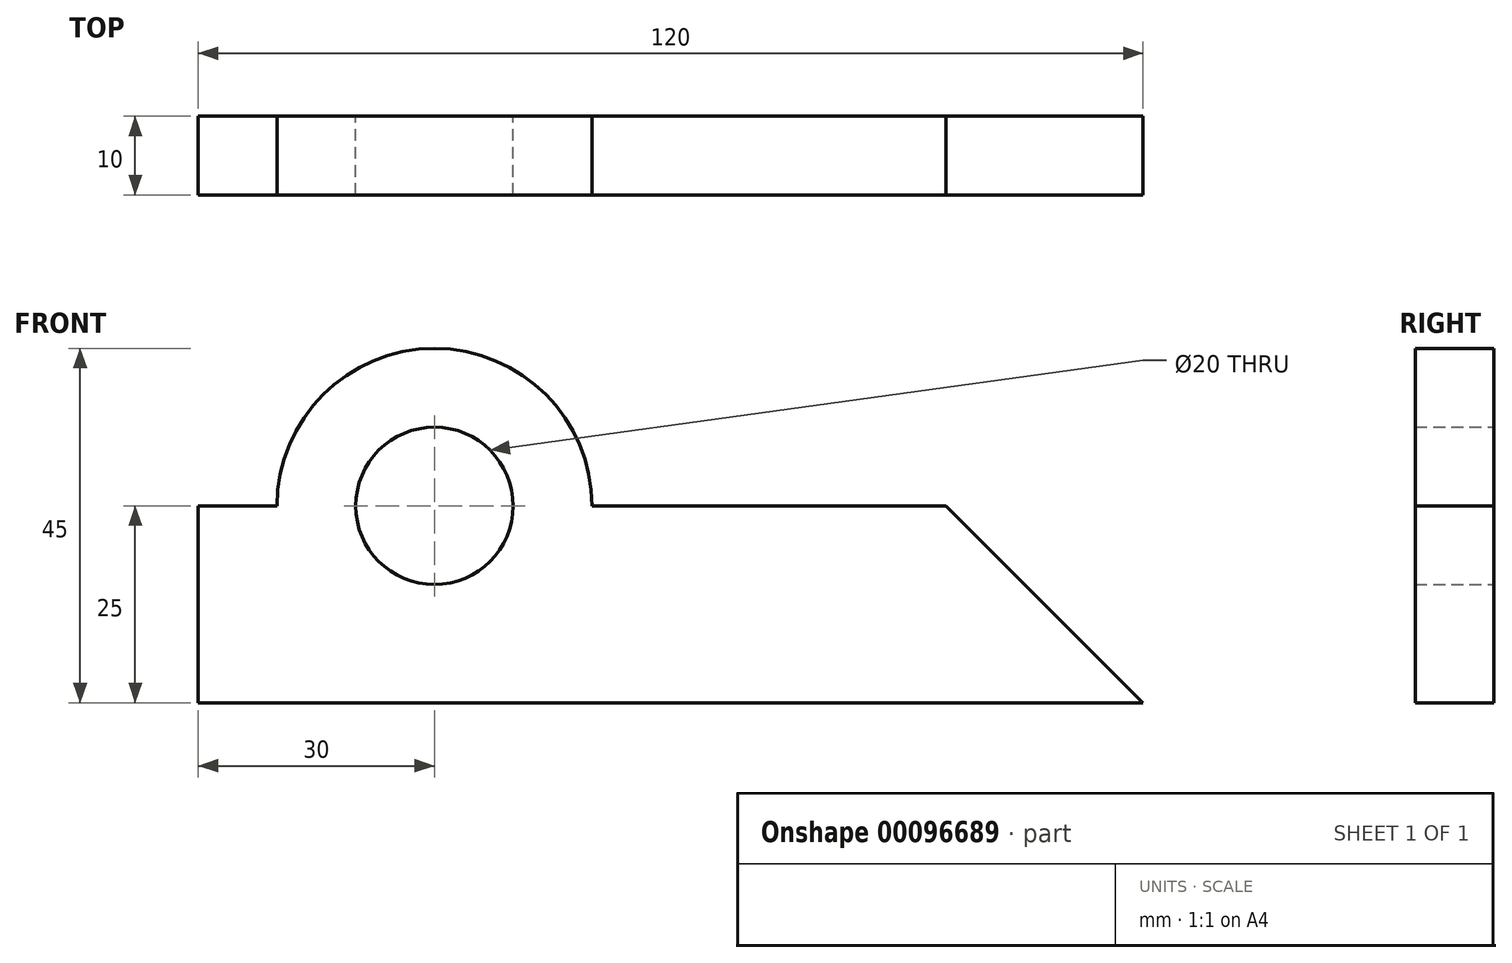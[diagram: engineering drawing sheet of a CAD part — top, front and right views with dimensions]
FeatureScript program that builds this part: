
annotation { "Feature Type Name" : "Feature", "Feature Type Description" : "" }
export const myFeature = defineFeature(function(context is Context, id is Id, definition is map)
    precondition{}
    {
        {
            var Q0;
            Q0=qCreatedBy(makeId("Front.planeOp"),FACE);
            var sketch = newSketch(context, id + "F0", { "sketchPlane" : qUnion([Q0])});
            skLineSegment(sketch, "E0", {"start": v(0, 0) * mm, "end": v(120, 0) * mm});
            skLineSegment(sketch, "E1", {"start": v(120, 0) * mm, "end": v(95, 25) * mm});
            skLineSegment(sketch, "E2", {"start": v(95, 25) * mm, "end": v(50, 25) * mm});
            skLineSegment(sketch, "E3", {"start": v(0, 0) * mm, "end": v(0, 25) * mm});
            skLineSegment(sketch, "E4", {"start": v(0, 25) * mm, "end": v(10, 25) * mm});
            skCircle(sketch, "E5", {"center": v(30, 25) * mm, "radius": 10 * mm});
            skArc(sketch, "E6", {"start": v(50, 25) * mm, "mid": v(30, 45) * mm, "end": v(10, 25) * mm});
            skSolve(sketch);
        }
        {
            var Q0;
            Q0 = qSketchRegion(id + "F0", true);
            extrude(context, id + "F1", {"entities" : qUnion([Q0]), "depth" : 10 * mm});
        }
    });
